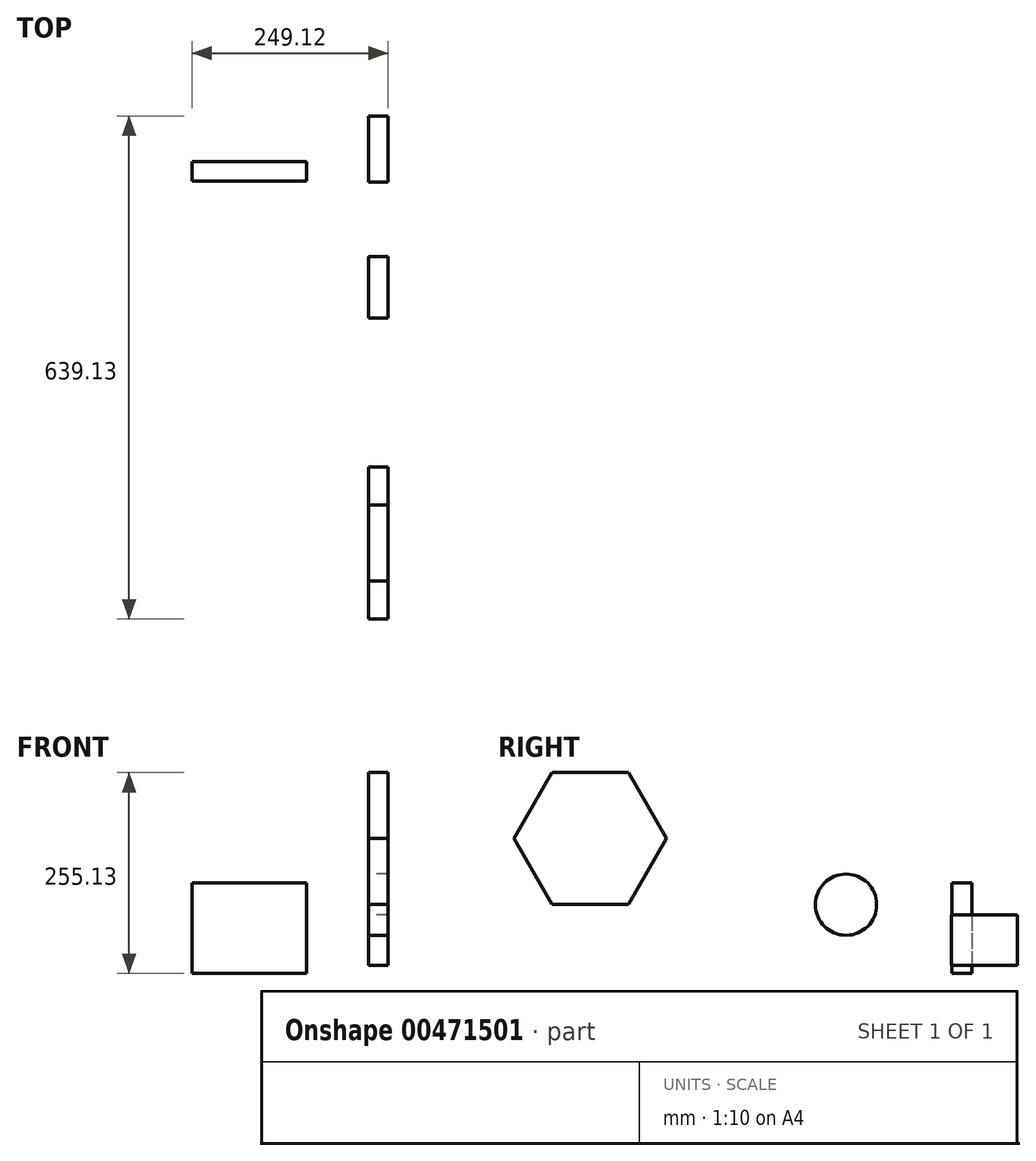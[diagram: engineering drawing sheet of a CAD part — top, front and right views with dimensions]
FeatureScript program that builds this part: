
annotation { "Feature Type Name" : "Feature", "Feature Type Description" : "" }
export const myFeature = defineFeature(function(context is Context, id is Id, definition is map)
    precondition{}
    {
        {
            var Q0;
            Q0=qCreatedBy(makeId("Right.planeOp"),FACE);
            var sketch = newSketch(context, id + "F0", { "sketchPlane" : qUnion([Q0])});
            skLineSegment(sketch, "E0.bottom", {"start": v(57.9, 45.37) * mm, "end": v(-25.86, 45.37) * mm});
            skLineSegment(sketch, "E0.top", {"start": v(57.9, -18.88) * mm, "end": v(-25.86, -18.88) * mm});
            skLineSegment(sketch, "E0.left", {"start": v(57.9, 45.37) * mm, "end": v(57.9, -18.88) * mm});
            skLineSegment(sketch, "E0.right", {"start": v(-25.86, 45.37) * mm, "end": v(-25.86, -18.88) * mm});
            skCircle(sketch, "E1", {"center": v(-159.65, 58.4) * mm, "radius": 38.88 * mm});
            skCircle(sketch, "E2.cCircle", {"center": v(-484.6, 142.46) * mm, "radius": 83.69 * mm, "construction": true});
            skLineSegment(sketch, "E2.0", {"start": v(-436.28, 58.77) * mm, "end": v(-532.92, 58.77) * mm});
            skLineSegment(sketch, "E2.1", {"start": v(-532.92, 58.77) * mm, "end": v(-581.23, 142.46) * mm});
            skLineSegment(sketch, "E2.2", {"start": v(-581.23, 142.46) * mm, "end": v(-532.92, 226.15) * mm});
            skLineSegment(sketch, "E2.3", {"start": v(-532.92, 226.15) * mm, "end": v(-436.28, 226.15) * mm});
            skLineSegment(sketch, "E2.4", {"start": v(-436.28, 226.15) * mm, "end": v(-387.97, 142.46) * mm});
            skLineSegment(sketch, "E2.5", {"start": v(-387.97, 142.46) * mm, "end": v(-436.28, 58.77) * mm});
            skPoint(sketch, "E2.0.midPoint", {"position": v(-484.6, 58.77) * mm});
            skSolve(sketch);
        }
        {
            var Q0;
            Q0 = qSketchRegion(id + "F0", true);
            extrude(context, id + "F1", {"entities" : qUnion([Q0]), "depth" : 25 * mm});
        }
        {
            var Q0;
            Q0=qCreatedBy(makeId("Front.planeOp"),FACE);
            var sketch = newSketch(context, id + "F2", { "sketchPlane" : qUnion([Q0])});
            skLineSegment(sketch, "E3.bottom", {"start": v(-224.12, 86.1) * mm, "end": v(-78.5, 86.1) * mm});
            skLineSegment(sketch, "E3.top", {"start": v(-224.12, -28.98) * mm, "end": v(-78.5, -28.98) * mm});
            skLineSegment(sketch, "E3.left", {"start": v(-224.12, 86.1) * mm, "end": v(-224.12, -28.98) * mm});
            skLineSegment(sketch, "E3.right", {"start": v(-78.5, 86.1) * mm, "end": v(-78.5, -28.98) * mm});
            skSolve(sketch);
        }
        {
            var Q0;
            Q0 = qSketchRegion(id + "F2", true);
            extrude(context, id + "F3", {"entities" : qUnion([Q0]), "depth" : 25 * mm});
        }
    });
